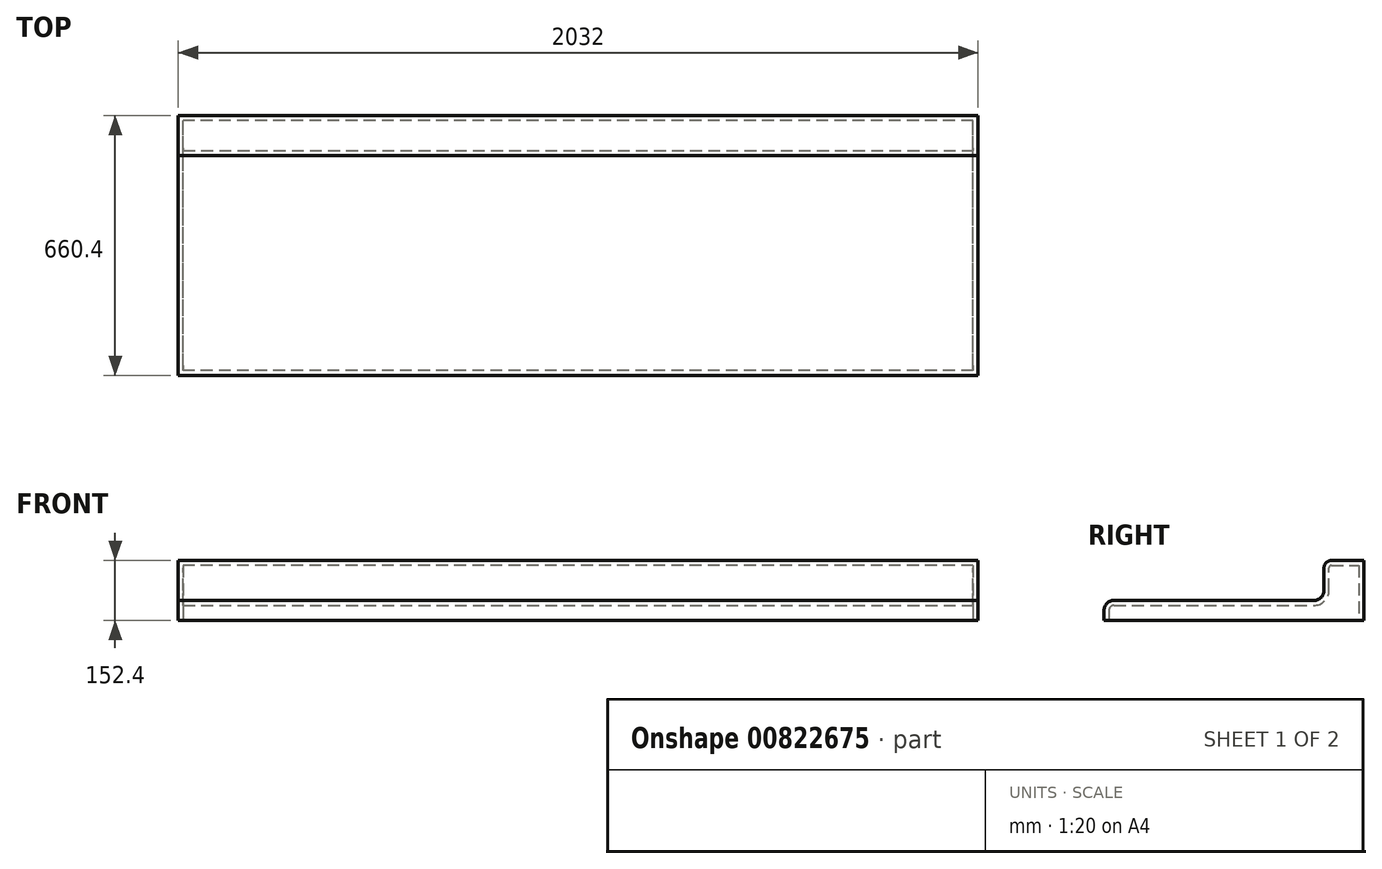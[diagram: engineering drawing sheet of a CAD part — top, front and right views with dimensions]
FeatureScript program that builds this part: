
annotation { "Feature Type Name" : "Feature", "Feature Type Description" : "" }
export const myFeature = defineFeature(function(context is Context, id is Id, definition is map)
    precondition{}
    {
        {
            var Q0;
            Q0=qCreatedBy(makeId("Right.planeOp"),FACE);
            var sketch = newSketch(context, id + "F0", { "sketchPlane" : qUnion([Q0])});
            skLineSegment(sketch, "E0.bottom", {"start": v(-162.6, 0) * mm, "end": v(345.4, 0) * mm});
            skLineSegment(sketch, "E0.top", {"start": v(-188, -50.8) * mm, "end": v(472.4, -50.8) * mm});
            skLineSegment(sketch, "E0.left", {"start": v(-188, -25.4) * mm, "end": v(-188, -50.8) * mm});
            skLineSegment(sketch, "E1.right", {"start": v(370.8, 25.4) * mm, "end": v(370.8, 82.55) * mm});
            skLineSegment(sketch, "E2.bottom", {"start": v(389.84, 101.6) * mm, "end": v(472.4, 101.6) * mm});
            skLineSegment(sketch, "E2.right", {"start": v(472.4, 101.6) * mm, "end": v(472.4, -50.8) * mm});
            skPoint(sketch, "E3.visualSharp", {"position": v(-188, 0) * mm});
            skArc(sketch, "E3.filletArc", {"start": v(-162.6, 0) * mm, "mid": v(-180.57, -7.44) * mm, "end": v(-188, -25.4) * mm});
            skPoint(sketch, "E4.visualSharp", {"position": v(370.8, 101.6) * mm});
            skArc(sketch, "E4.filletArc", {"start": v(389.84, 101.6) * mm, "mid": v(376.37, 96.02) * mm, "end": v(370.8, 82.55) * mm});
            skPoint(sketch, "E5.visualSharp", {"position": v(370.8, 0) * mm});
            skArc(sketch, "E5.filletArc", {"start": v(345.4, 0) * mm, "mid": v(363.35, 7.44) * mm, "end": v(370.8, 25.4) * mm});
            skSolve(sketch);
        }
        {
            var Q0;
            Q0 = qSketchRegion(id + "F0", true);
            extrude(context, id + "F1", {"entities" : qUnion([Q0]), "depth" : 2032 * mm, "offsetDistance" : 25.4 * mm});
        }
        {
            var Q0;
            Q0=makeQuery(id+"F1.opExtrude","SWEPT_FACE",FACE,{"disambiguationData":[OSD([sQuery(id+"F0.wireOp",EDGE,"E0.top")])]});
            shell(context, id + "F2", {"entities" : qUnion([Q0]), "thickness" : 12.7 * mm});
        }
    });
